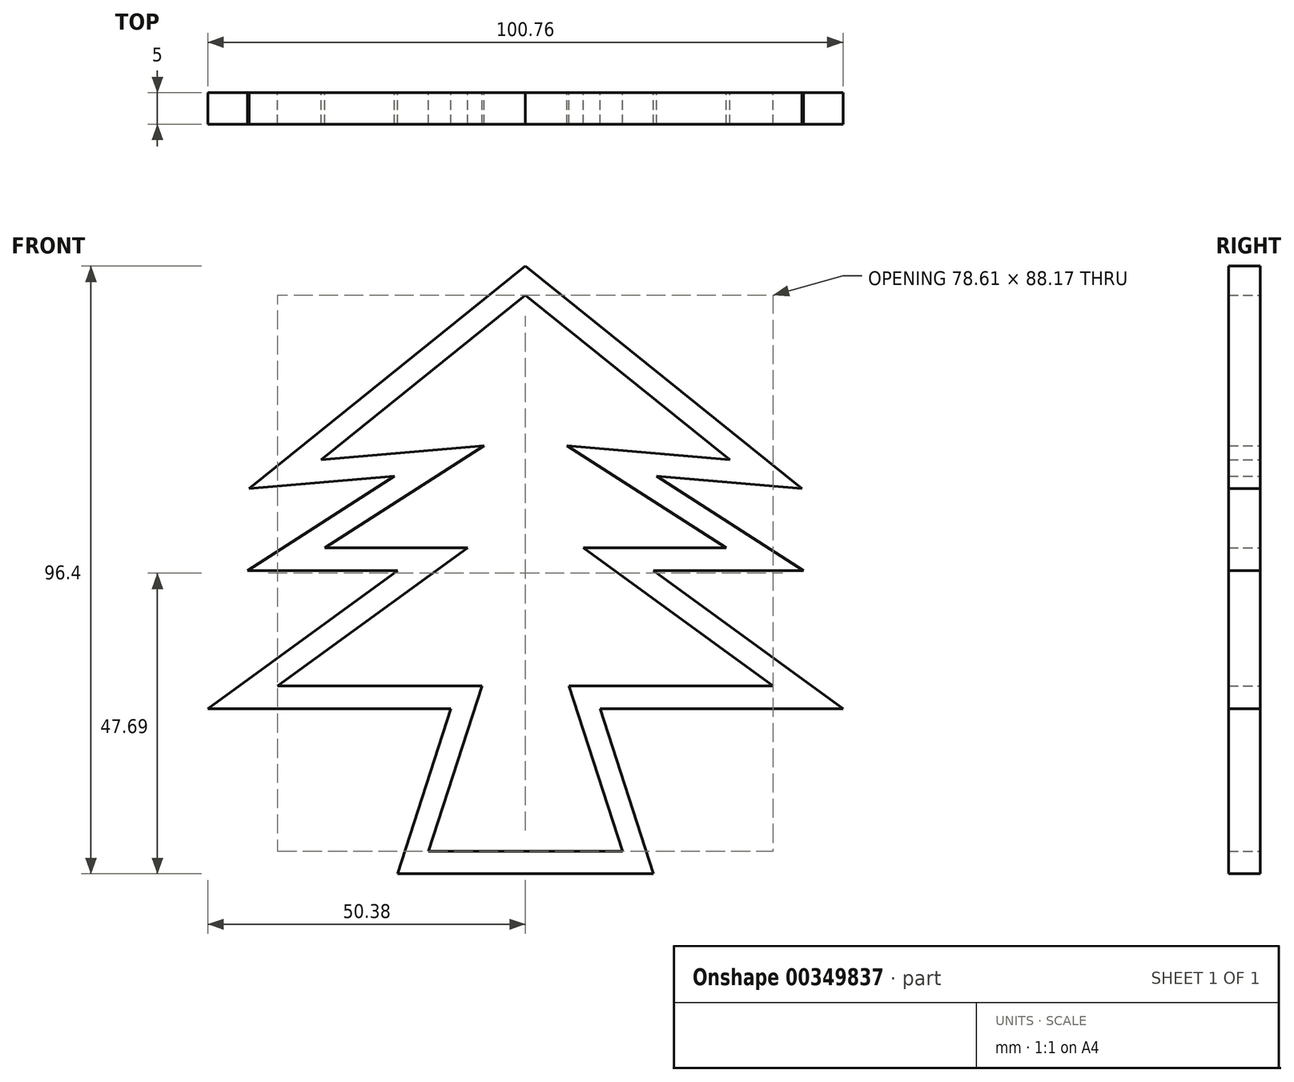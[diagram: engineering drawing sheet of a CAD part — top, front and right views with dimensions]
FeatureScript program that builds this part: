
annotation { "Feature Type Name" : "Feature", "Feature Type Description" : "" }
export const myFeature = defineFeature(function(context is Context, id is Id, definition is map)
    precondition{}
    {
        {
            var Q0;
            Q0=qCreatedBy(makeId("Front.planeOp"),FACE);
            var sketch = newSketch(context, id + "F0", { "sketchPlane" : qUnion([Q0])});
            skLineSegment(sketch, "E0", {"start": v(0, -48.09) * mm, "end": v(-15.37, -48.09) * mm});
            skLineSegment(sketch, "E1", {"start": v(-15.37, -48.09) * mm, "end": v(-6.9, -21.89) * mm});
            skLineSegment(sketch, "E2", {"start": v(-6.9, -21.89) * mm, "end": v(-39.3, -21.89) * mm});
            skLineSegment(sketch, "E3", {"start": v(-39.3, -21.89) * mm, "end": v(-9.18, 0) * mm});
            skLineSegment(sketch, "E4", {"start": v(-9.18, 0) * mm, "end": v(-31.84, 0) * mm});
            skLineSegment(sketch, "E5", {"start": v(-31.84, 0) * mm, "end": v(-6.6, 16.2) * mm});
            skLineSegment(sketch, "E6", {"start": v(-6.6, 16.2) * mm, "end": v(-32.4, 14) * mm});
            skLineSegment(sketch, "E7", {"start": v(-32.4, 14) * mm, "end": v(0, 40.09) * mm});
            skLineSegment(sketch, "E8.0", {"start": v(-43.84, 9.4) * mm, "end": v(0, 44.7) * mm});
            skLineSegment(sketch, "E8.1", {"start": v(-20.79, 11.38) * mm, "end": v(-43.84, 9.4) * mm});
            skLineSegment(sketch, "E8.2", {"start": v(-44.11, -3.6) * mm, "end": v(-20.79, 11.38) * mm});
            skLineSegment(sketch, "E8.3", {"start": v(-20.26, -3.6) * mm, "end": v(-44.11, -3.6) * mm});
            skLineSegment(sketch, "E8.4", {"start": v(0, -51.69) * mm, "end": v(-20.32, -51.69) * mm});
            skLineSegment(sketch, "E8.5", {"start": v(-20.32, -51.69) * mm, "end": v(-11.85, -25.49) * mm});
            skLineSegment(sketch, "E8.6", {"start": v(-11.85, -25.49) * mm, "end": v(-50.38, -25.49) * mm});
            skLineSegment(sketch, "E8.7", {"start": v(-50.38, -25.49) * mm, "end": v(-20.26, -3.6) * mm});
            skLineSegment(sketch, "E9.MirrorCS", {"start": v(0, -48.09) * mm, "end": v(15.37, -48.09) * mm});
            skLineSegment(sketch, "E10.MirrorCS", {"start": v(44.11, -3.6) * mm, "end": v(20.79, 11.38) * mm});
            skLineSegment(sketch, "E11.MirrorCS", {"start": v(20.32, -51.69) * mm, "end": v(11.85, -25.49) * mm});
            skLineSegment(sketch, "E12.MirrorCS", {"start": v(15.37, -48.09) * mm, "end": v(6.9, -21.89) * mm});
            skLineSegment(sketch, "E13.MirrorCS", {"start": v(20.79, 11.38) * mm, "end": v(43.84, 9.4) * mm});
            skLineSegment(sketch, "E14.MirrorCS", {"start": v(11.85, -25.49) * mm, "end": v(50.38, -25.49) * mm});
            skLineSegment(sketch, "E15.MirrorCS", {"start": v(0, -51.69) * mm, "end": v(20.32, -51.69) * mm});
            skLineSegment(sketch, "E16.MirrorCS", {"start": v(39.3, -21.89) * mm, "end": v(9.18, 0) * mm});
            skLineSegment(sketch, "E17.MirrorCS", {"start": v(31.84, 0) * mm, "end": v(6.6, 16.2) * mm});
            skLineSegment(sketch, "E18.MirrorCS", {"start": v(20.26, -3.6) * mm, "end": v(44.11, -3.6) * mm});
            skLineSegment(sketch, "E19.MirrorCS", {"start": v(6.9, -21.89) * mm, "end": v(39.3, -21.89) * mm});
            skLineSegment(sketch, "E20.MirrorCS", {"start": v(50.38, -25.49) * mm, "end": v(20.26, -3.6) * mm});
            skLineSegment(sketch, "E21.MirrorCS", {"start": v(6.6, 16.2) * mm, "end": v(32.4, 14) * mm});
            skLineSegment(sketch, "E22.MirrorCS", {"start": v(9.18, 0) * mm, "end": v(31.84, 0) * mm});
            skLineSegment(sketch, "E23.MirrorCS", {"start": v(32.4, 14) * mm, "end": v(0, 40.09) * mm});
            skLineSegment(sketch, "E24.MirrorCS", {"start": v(43.84, 9.4) * mm, "end": v(0, 44.7) * mm});
            skSolve(sketch);
        }
        {
            var Q0;
            Q0=makeQuery(id+"F0.imprint","IMPRINT",FACE,{"disambiguationData":[TD([[makeQuery(id+"F0.imprint","IMPRINT",EDGE,{"derivedFrom":sQuery(id+"F0.wireOp",EDGE,"E0")}),1.0]])]});
            extrude(context, id + "F1", {"entities" : qUnion([Q0]), "depth" : 5 * mm});
        }
    });
